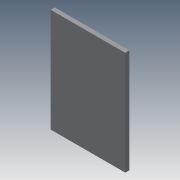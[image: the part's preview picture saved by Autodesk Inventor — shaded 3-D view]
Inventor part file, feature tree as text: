
AUTODESK INVENTOR PART (.ipt)
format: ipt  version: 2015 (Build 190159000, 159)  size: 73,216 bytes
history: native  units: mm
features: extrude x1, sketch x1
ambient origin geometry x8: Origin, YZ Plane, XZ Plane, XY Plane, X Axis, Y Axis, Z Axis, Center Point
bodies: Solid1 (feature_tree)
feature tree (2):
  extrude  "Extrusion1"  Depth=180.0mm
  sketch  "Sketch1"  dims[d1=250.0mm d2=180.0mm d3=10.0mm d4=0.0mm]
